# Revit family: CAME_Турникет_Трипод_STILE_400
name_source: partatom
category: Специальное оборудование
units: mm (PartAtom-declared; Revit-internal decimal feet)

## family parameters
Всегда вертикально = Да
На основе рабочей плоскости = Нет
Общий = Нет
При загрузке вырезать с полостями = Нет
Размер круглого соединителя = Использовать диаметр
Тип детали = Нормальный
Точка расчета площади = Нет

## types (1)
- CAME_Турникет_Трипод_STILE_400
    ADSK_URL документации изделия = https://camerussia.com
    ADSK_URL страницы изделия = https://camerussia.com
    ADSK_Версия Revit = 2019
    ADSK_Версия семейства = 1.0
    ADSK_Группирование = STILE
    ADSK_Единица измерения = шт.
    ADSK_Завод-изготовитель = CAME
    ADSK_Классификация нагрузок = Прочее
    ADSK_Код изделия = Код КСР 26.30.50.119.61.2.07.09
    ADSK_Количество = 1
    ADSK_Количество фаз = 1
    ADSK_Коэффициент мощности = 0.96
    ADSK_Марка = АРТ:001PSMM400E-01
    ADSK_Масса = 22
    ADSK_Масса_Текст = 22 кг
    ADSK_Наименование = Турникет-трипод электромеханический STILE 400
    ADSK_Наименование краткое = Турникет-трипод STILE 400
    ADSK_Напряжение = 230 В
    ADSK_Номинальная мощность = 60 Вт
    ADSK_Обозначение = ТУ 26.30.50-001-89603926-2021
    ADSK_Полная мощность = 63 В·А
    ADSK_Размер_Высота = 250 мм
    ADSK_Размер_Глубина = 500 мм
    ADSK_Размер_Ширина = 770 мм
    BL_BIM library = https://bimlib.pro
    CAME_Диапазон рабочих температур (°C) = -20 ÷ +68
    CAME_Интенсивность использования (%) = ИНТЕНСИВНОЕ
    CAME_Класс защиты (IP) = 54
    CAME_Максимальное количество проходов в минуту = 46
    CAME_Напряжение электропитания двигателя (В) = 24 В
    CAME_Тип механизма турникета = электромеханический
    URL = https://camerussia.com
    Группа модели = Турникеты
    Изготовитель = CAME
    Минимальная ширина проема = 790 мм
    Описание = Турникет-трипод электромеханический. Корпус и преграды из нержавеющей стали AISI 304. Оснащен платой управления и светодиодными указателями прохода. Стандартные преграждающие планки с гидравлической доводкой и автоматической разблокировкой при отключении электроэнергии. Встроенный блок питания.
